# Revit family: Drain_Adjustable_6_Inch_Isolation_Deck-Zurn-Z625
name_source: partatom
category: Plumbing Fixtures
units: mm (PartAtom-declared; Revit-internal decimal feet)

## family parameters
Always vertical = Yes
Cut with Voids When Loaded = No
Maintain Annotation Orientation = No
Part Type = Normal
Room Calculation Point = No
Round Connector Dimension = Use Radius
Shared = No
Work Plane-Based = No

## types (14) — shared parameters
Approx. Weight (Lbs) = 42 "
Assembly Code = D2030300
CW Connection = No
Default Elevation = 20 "
Description = ADJUSTABLE ISOLATION DECK DRAIN
Enter Value-Frame Adjustment Height = 1.5 "
Frame Adjustment Height = 1.5 "
Grate Open Area = 9 "
HW Connection = No
Main Material = Iron - Zurn - Cast - Painted - Blue
Manufacturer = Zurn Water, LLC
Manufacturer Brand = Zurn
Model = Z625
Modified Date = 12/19/2025
Product Documentation Link = https://files.zurn.com
Product Installation Sheet URL = https://files.zurn.com
Product Page URL = https://www.zurn.com
Product data URL = https://www.bimobject.com
Top Plate Width = 6.188 "
URL = www.zurn.com
Vent Connection = No
WFU = 1
Waste Connection = Yes
Width = 15 "
zero-valued in all types: CWFU, HWFU

## per-type parameters (varying)
| type | Body Height_E | Grate Material | Pipe Size_A Inside Radius | Pipe Size_A Nominal Radius | Pipe Size_A Outer Radius | Type Comments |
| ZB625-2NH | 5.25 " | Bronze - Zurn - Polished | 1.034 " | 1 " | 1.188 " | ZB625-2 Inch No-Hub Outlet |
| ZB625-2NL | 4.625 " | Bronze - Zurn - Polished | 1.034 " | 1 " | 1.188 " | ZB625-2 Inch Neo-Loc Outelt |
| ZB625-3NH | 5.25 " | Bronze - Zurn - Polished | 1.534 " | 1.5 " | 1.75 " | ZB625-3 Inch No-Hub Outlet |
| ZB625-3NL | 4.625 " | Bronze - Zurn - Polished | 1.534 " | 1.5 " | 1.75 " | ZB625-3 Inch Neo-Loc Outelt |
| ZB625-4NH | 5.25 " | Bronze - Zurn - Polished | 2.013 " | 2 " | 2.25 " | ZB625-4 Inch No-Hub Outlet |
| ZB625-4NL | 4.625 " | Bronze - Zurn - Polished | 2.013 " | 2 " | 2.25 " | ZB625-4 Inch Neo-Loc Outelt |
| ZB625-6NH | 5.25 " | Bronze - Zurn - Polished | 3.033 " | 3 " | 3.313 " | ZB625-6 Inch No-Hub Outlet |
| ZN625-2NH | 5.25 " | Bronze - Zurn - Polished Nickel | 1.034 " | 1 " | 1.188 " | ZN625-2 Inch No-Hub Outlet |
| ZN625-2NL | 4.625 " | Bronze - Zurn - Polished Nickel | 1.034 " | 1 " | 1.188 " | ZN625-2 Inch Neo-Loc Outelt |
| ZN625-3NH | 5.25 " | Bronze - Zurn - Polished Nickel | 1.534 " | 1.5 " | 1.75 " | ZN625-3 Inch No-Hub Outlet |
| ZN625-3NL | 4.625 " | Bronze - Zurn - Polished Nickel | 1.534 " | 1.5 " | 1.75 " | ZN625-3 Inch Neo-Loc Outelt |
| ZN625-4NH | 5.25 " | Bronze - Zurn - Polished Nickel | 2.013 " | 2 " | 2.25 " | ZN625-4 Inch No-Hub Outlet |
| ZN625-4NL | 4.625 " | Bronze - Zurn - Polished Nickel | 2.013 " | 2 " | 2.25 " | ZN625-4 Inch Neo-Loc Outelt |
| ZN625-6NH | 5.25 " | Bronze - Zurn - Polished Nickel | 3.033 " | 3 " | 3.313 " | ZN625-6 Inch No-Hub Outlet |

## geometry (parser evidence)
native form markers: Sweep x2
no freeform markers — native parametric forms only
